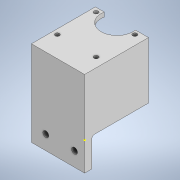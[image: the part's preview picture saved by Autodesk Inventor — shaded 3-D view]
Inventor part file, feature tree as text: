
AUTODESK INVENTOR PART (.ipt)
format: ipt  version: 2022 (Build 260153000, 153)  size: 215,552 bytes
history: native  units: mm
features: sketch x11, extrude x7, fillet x3, hole x2, other x1, projected_geometry x1
ambient origin geometry x8: Origin, YZ Plane, XZ Plane, XY Plane, X Axis, Y Axis, Z Axis, Center Point
bodies: Body1 (feature_tree)
feature tree (25):
  other  "ソリッド1"
  extrude  "押し出し1"  Depth=44.5mm
  extrude  "押し出し2"  Depth=34.0mm
  extrude  "押し出し3"  Depth=39.5mm TaperAngle=0.0deg
  extrude  "押し出し4"  Depth=3.0mm
  hole  "穴1"  [1 undecoded]
  fillet  "フィレット1"  Radius=33.5mm
  fillet  "フィレット2"  Radius=50.0mm
  sketch  "スケッチ7"
  extrude  "押し出し5"  Depth=43.5mm TaperAngle=0.0deg
  hole  "穴3"  [1 undecoded]
  extrude  "押し出し6"  Depth=2.0mm
  fillet  "フィレット4"  Radius=17.0mm
  extrude  "押し出し9"  Depth=3.0mm TaperAngle=0.0deg
  sketch  "スケッチ18"
  sketch  "スケッチ1"
  sketch  "スケッチ2"
  sketch  "スケッチ3"
  sketch  "スケッチ4"
  sketch  "スケッチ5"
  sketch  "スケッチ8"
  sketch  "スケッチ9"
  sketch  "スケッチ11"
  projected_geometry  "投影ループ1"
  sketch  "スケッチ17"
note: 2 required parameter values undecoded (feature->parameter linkage not recoverable at this tier; creation-order binding heuristic only, values carry confidence <= 0.55)
